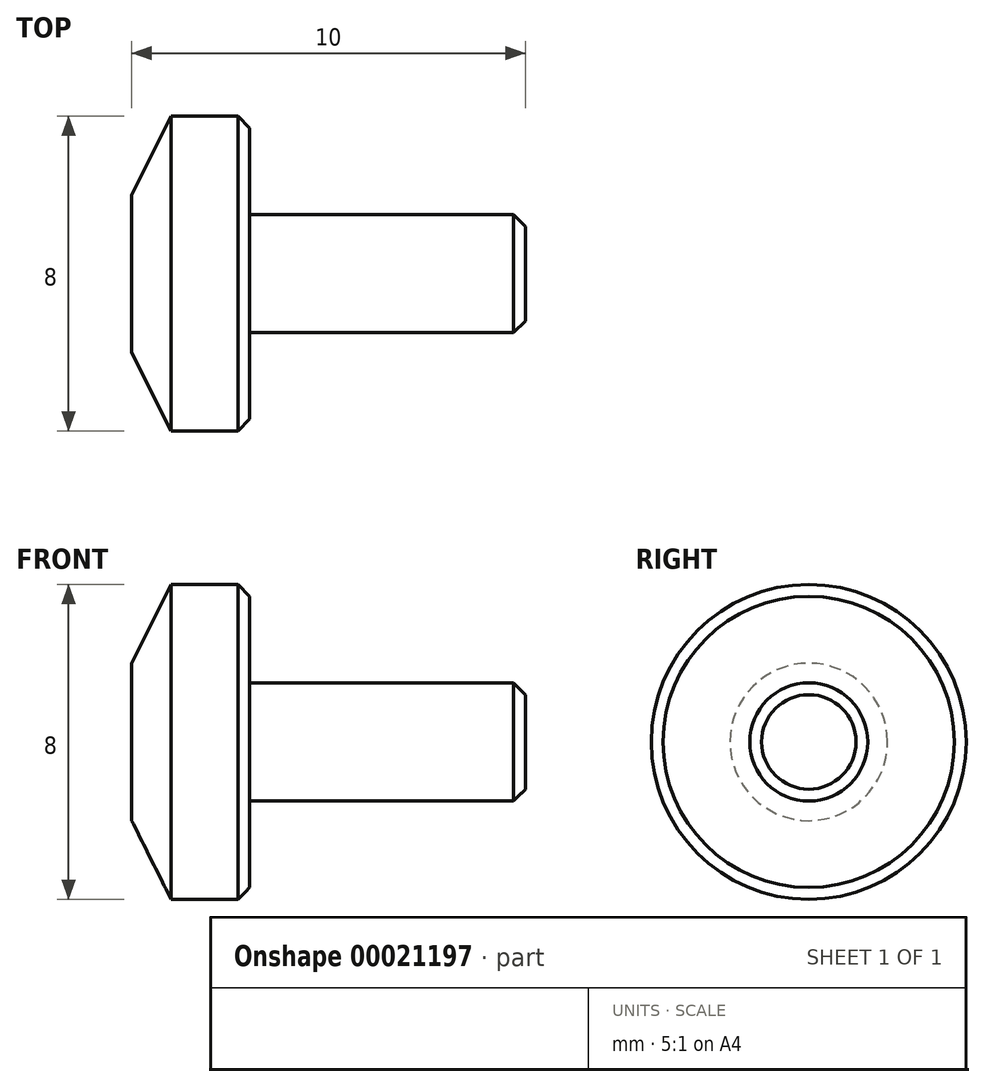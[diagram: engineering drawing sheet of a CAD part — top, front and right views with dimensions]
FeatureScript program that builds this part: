
annotation { "Feature Type Name" : "Feature", "Feature Type Description" : "" }
export const myFeature = defineFeature(function(context is Context, id is Id, definition is map)
    precondition{}
    {
        {
            var Q0;
            Q0=qCreatedBy(makeId("Right.planeOp"),FACE);
            var sketch = newSketch(context, id + "F0", { "sketchPlane" : qUnion([Q0])});
            skCircle(sketch, "E0", {"center": v(0, 0) * mm, "radius": 4 * mm});
            skSolve(sketch);
        }
        {
            var Q0;
            Q0=qSketchRegion(id+"F0",true);
            extrude(context, id + "F1", {"entities" : qUnion([Q0]), "oppositeDirection" : true, "depth" : 3 * mm});
        }
        {
            var Q0;
            Q0=makeQuery(id+"F1.opExtrude","CAP_EDGE",EDGE,{"disambiguationData":[OSD([sQuery(id+"F0.wireOp",EDGE,"E0")])],"isStart":false});
            chamfer(context, id + "F2", {"entities" : qUnion([Q0]), "chamferType" : ChamferType.TWO_OFFSETS, "width1" : 1 * mm, "oppositeDirection" : false, "width2" : 2 * mm, "tangentPropagation" : true});
        }
        {
            var Q0;
            Q0=makeQuery(id+"F1.opExtrude","CAP_FACE",FACE,{"disambiguationData":[OSD([sQuery(id+"F0.wireOp",EDGE,"E0")])],"isStart":true});
            var sketch = newSketch(context, id + "F3", { "sketchPlane" : qUnion([Q0])});
            skCircle(sketch, "E1", {"center": v(0, 0) * mm, "radius": 1.5 * mm});
            skSolve(sketch);
        }
        {
            var Q0;
            Q0=qSketchRegion(id+"F3",true);
            extrude(context, id + "F4", {"entities" : qUnion([Q0]), "operationType" : NewBodyOperationType.ADD, "depth" : 7 * mm});
        }
        {
            var Q0;
            Q0=makeQuery(id+"F4.opExtrude","CAP_EDGE",EDGE,{"disambiguationData":[OSD([sQuery(id+"F3.wireOp",EDGE,"E1")])],"isStart":false});
            var Q1;
            Q1=makeQuery(id+"F1.opExtrude","CAP_EDGE",EDGE,{"disambiguationData":[OSD([sQuery(id+"F0.wireOp",EDGE,"E0")])],"isStart":true});
            chamfer(context, id + "F5", {"entities" : qUnion([Q0, Q1]), "width" : 0.3 * mm, "tangentPropagation" : true});
        }
    });
